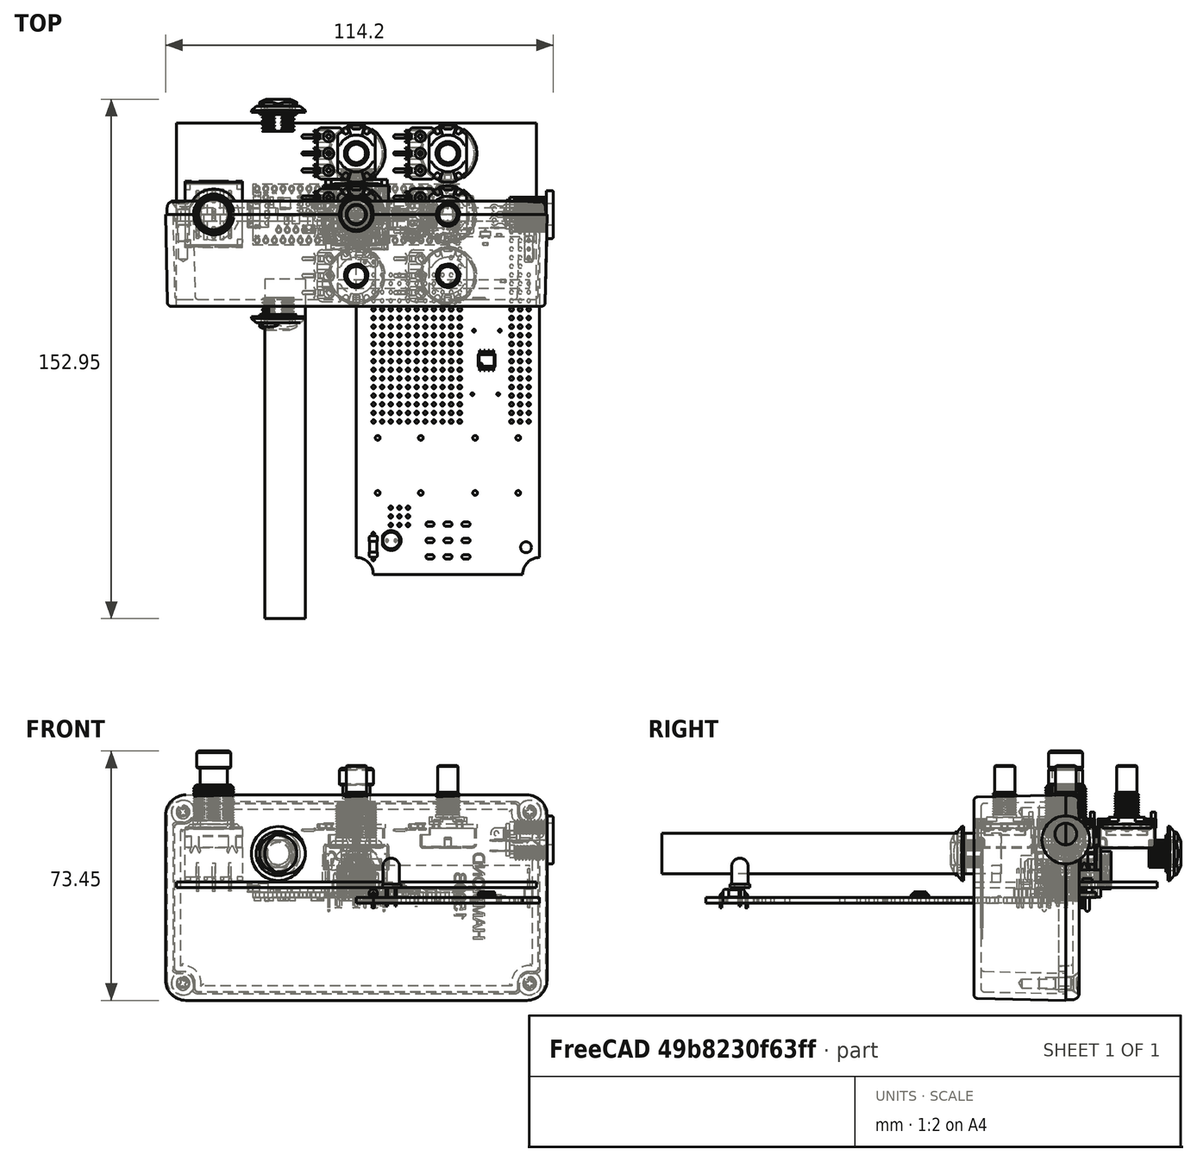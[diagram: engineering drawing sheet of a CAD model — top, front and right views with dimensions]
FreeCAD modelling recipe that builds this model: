
FCSTD DOCUMENT  (FreeCAD 0.19R24267 +148 (Git))
Label: 1590Balt
License: All rights reserved
LicenseURL: http://en.wikipedia.org/wiki/All_rights_reserved
objects: Part::Feature×58, App::Link×50, App::Part×9, Part::Box×3, Part::Compound2×1, Part::Cylinder×1, PartDesign::CoordinateSystem×1, Sketcher::SketchObject×1
note: 64 computed .brp shape members not serialized (recipe doc carries the construction recipe); baked Part::Feature solids carry a one-line shape summary decoded from their .brp

FEATURE [Part::Feature] Part__Feature  label="1590B BOX"
  Placement = pos=(0,0,0) rot=(-1,0,0;1.5708rad)
  shape: bbox 112.4 x 261 x 60.52 mm, 255 faces (baked)
FEATURE [Part::Feature] Part__Feature001  label="1590B-BS LID"
  Placement = pos=(0,0,0) rot=(0,0.707107,-0.707107;3.14159rad)
  shape: bbox 112.4 x 6.014 x 61.03 mm, 68 faces (baked)
FEATURE [Part::Feature] Part__Feature002  label="SC530 (screw #6-32X 1_2' FH)"
  Placement = pos=(-51.05,1.5362,25.25) rot=(0,1,0;0.650238rad)
  shape: bbox 6.871 x 11.85 x 6.871 mm, 25 faces (baked)
FEATURE [Part::Feature] Part__Feature003  label="SC530 (screw #6-32X 1_2' FH)001"
  Placement = pos=(-51.05,1.5362,-25.25) rot=(0,-1,0;0.529817rad)
  shape: bbox 6.871 x 11.85 x 6.871 mm, 25 faces (baked)
FEATURE [Part::Feature] Part__Feature004  label="SC530 (screw #6-32X 1_2' FH)002"
  Placement = pos=(51.05,1.5362,25.25) rot=(0,0,1;0rad)
  shape: bbox 6.871 x 11.85 x 6.871 mm, 25 faces (baked)
FEATURE [Part::Feature] Part__Feature005  label="SC530 (screw #6-32X 1_2' FH)003"
  Placement = pos=(51.05,1.5362,-25.25) rot=(0,0,1;0rad)
  shape: bbox 6.871 x 11.85 x 6.871 mm, 25 faces (baked)
FEATURE [App::Part] _590B  label="1590B"
  Group = -> [Part__Feature,Part__Feature001,Part__Feature002,Part__Feature003,Part__Feature004,Part__Feature005]
  Origin = -> Origin
  Placement = pos=(0,0,0) rot=(1,0,0;-1.5708rad)
FEATURE [Part::Feature] Part__Feature009  label="DC jack v1"
  Placement = pos=(58,0,17) rot=(0.57735,-0.57735,-0.57735;2.0944rad)
  shape: bbox 18.72 x 15.28 x 15.28 mm, 264 faces, 6 solids (baked)
FEATURE [Part::Feature] Part__Feature010  label="SF17020F-0302-21R-L v2"
  Placement = pos=(-42,0,5) rot=(0,0,-1;1.5708rad)
  shape: bbox 17.02 x 19.62 x 41.22 mm, 460 faces, 13 solids (baked)
FEATURE [Part::Box] Box  label="PCB"
  AttacherType = Attacher::AttachEngine3D
  Height = 1.6
  Length = 106
  Placement = pos=(-53,-27,3) rot=(0,0,1;0rad)
  Width = 54
FEATURE [Part::Box] Box002  label="header"
  AttacherType = Attacher::AttachEngine3D
  Height = 5
  Length = 61
  Placement = pos=(-10,-21.7,4.6) rot=(0,0,1;0rad)
  Width = 2.5
FEATURE [Part::Box] Box003  label="header001"
  AttacherType = Attacher::AttachEngine3D
  Height = 5
  Length = 61
  Placement = pos=(-10,-6.4,4.6) rot=(0,0,1;0rad)
  Width = 2.5
FEATURE [Part::Feature] Part__Feature037  label="RV16AF-20 v3"
  Placement = pos=(27,18,13) rot=(0,0,-1;1.5708rad)
  shape: bbox 24.95 x 17.82 x 24.32 mm, 272 faces, 6 solids (baked)
FEATURE [Part::Feature] Part__Feature038  label="RV16AF-20 v004"
  Placement = pos=(27,-6e-15,13) rot=(0,0,-1;1.5708rad)
  shape: bbox 24.95 x 17.82 x 24.32 mm, 272 faces, 6 solids (baked)
FEATURE [Part::Feature] Part__Feature039  label="RV16AF-20 v005"
  Placement = pos=(27,-18,13) rot=(0,0,-1;1.5708rad)
  shape: bbox 24.95 x 17.82 x 24.32 mm, 272 faces, 6 solids (baked)
FEATURE [Part::Feature] Part__Feature040  label="RV16AF-20 v006"
  Placement = pos=(4e-15,18,13) rot=(0,0,-1;1.5708rad)
  shape: bbox 24.95 x 17.82 x 24.32 mm, 272 faces, 6 solids (baked)
FEATURE [Part::Feature] Part__Feature041  label="RV16AF-20 v007"
  Placement = pos=(0,-1.2e-14,13) rot=(0,0,-1;1.5708rad)
  shape: bbox 24.95 x 17.82 x 24.32 mm, 272 faces, 6 solids (baked)
FEATURE [Part::Feature] Part__Feature042  label="RV16AF-20 v008"
  Placement = pos=(4e-15,-18,13) rot=(0,0,-1;1.5708rad)
  shape: bbox 24.95 x 17.82 x 24.32 mm, 272 faces, 6 solids (baked)
FEATURE [Part::Feature] Part__Feature043  label="NMJ nut washer v1"
  Placement = pos=(-23,-29.5,13) rot=(1,0,0;1.5708rad)
  shape: bbox 15.9 x 2.5 x 15.9 mm, 9 faces (baked)
FEATURE [Part::Feature] Part__Feature044  label="NMJ nut v1"
  Placement = pos=(-23,-34,13) rot=(-1,0,0;1.5708rad)
  shape: bbox 12.72 x 9.727 x 12.72 mm, 70 faces (baked)
FEATURE [Part::Feature] Part__Feature045  label="NMJ nut washer v002"
  Placement = pos=(-23,29.5,13) rot=(0,0.707107,0.707107;3.14159rad)
  shape: bbox 15.9 x 2.5 x 15.9 mm, 9 faces (baked)
FEATURE [Part::Feature] Solid
  shape: bbox 15 x 11.43 x 1.06 mm, 146 faces (baked)
FEATURE [Part::Feature] Solid001
  shape: bbox 62.51 x 17.83 x 5.318 mm, 3668 faces (baked)
FEATURE [Part::Compound2] Compound  label="CIRCUIT BOARD,TEENSY 4.1"
  Links = -> [Solid,Solid001]
  Placement = pos=(20.5,-12.8,9.6) rot=(0,0,1;3.14159rad)
FEATURE [Part::Feature] Part__Feature046  label="NMJ nut v002"
  Placement = pos=(-23,34,13) rot=(0,0.707107,-0.707107;3.14159rad)
  shape: bbox 12.72 x 9.727 x 12.72 mm, 70 faces (baked)
FEATURE [Part::Cylinder] Cylinder
  Angle = 360
  AttacherType = Attacher::AttachEngine3D
  Height = 100
  Placement = pos=(-21,-19,13) rot=(1,0,0;1.5708rad)
  Radius = 6
FEATURE [PartDesign::CoordinateSystem] Local_CS_9c2f
  AttacherType = Attacher::AttachEngine3D
  MapMode = 2
  Support = -> [X_Axis001]
FEATURE [Part::Feature] Pcb_9c2f
  shape: bbox 54 x 106 x 1.6 mm, 374 faces (baked)
FEATURE [Sketcher::SketchObject] PCB_Sketch_9c2f
  FullyConstrained = false
  sketch-geometry (8):
    g0: LineSegment StartX=5 StartY=-106 StartZ=0 EndX=49 EndY=-106 EndZ=0
    g1: LineSegment StartX=54 StartY=-5 StartZ=0 EndX=54 EndY=-101 EndZ=0
    g2: LineSegment StartX=5 StartY=0 StartZ=0 EndX=49 EndY=-2e-16 EndZ=0
    g3: LineSegment StartX=0 StartY=-101 StartZ=0 EndX=0 EndY=-5 EndZ=0
    g4: ArcOfCircle CenterX=54 CenterY=-106 CenterZ=0 NormalX=0 NormalY=0 NormalZ=-1 AngleXU=-6.42331e-08 Radius=5 StartAngle=0 EndAngle=1.5708
    g5: ArcOfCircle CenterX=54 CenterY=-3.21166e-07 CenterZ=0 NormalX=0 NormalY=0 NormalZ=-1 AngleXU=-1.5708 Radius=5 StartAngle=0 EndAngle=1.5708
    g6: ArcOfCircle CenterX=3.21166e-07 CenterY=-3.21166e-07 CenterZ=0 NormalX=0 NormalY=0 NormalZ=-1 AngleXU=3.14159 Radius=5 StartAngle=0 EndAngle=1.5708
    g7: ArcOfCircle CenterX=3.21166e-07 CenterY=-106 CenterZ=0 NormalX=0 NormalY=0 NormalZ=-1 AngleXU=1.5708 Radius=5 StartAngle=0 EndAngle=1.5708
  constraints (8):
    c: Coincident(g3,g7)
    c: Coincident(g3,g6)
    c: Coincident(g0,g7)
    c: Coincident(g2,g6)
    c: Coincident(g0,g4)
    c: Coincident(g2,g5)
    c: Coincident(g1,g4)
    c: Coincident(g1,g5)
FEATURE [App::Part] Board_Geoms_9c2f
  Group = -> [Pcb_9c2f,PCB_Sketch_9c2f]
  Origin = -> Origin002
FEATURE [Part::Feature] Shape  label="C21_C_0603_1608Metric_0bb367dbc1dc"
  Placement = pos=(38.05,-8.6,0) rot=(0,0,1;0rad)
  shape: bbox 1.6 x 0.8 x 0.8 mm, 28 faces (baked)
FEATURE [Part::Feature] Shape001  label="R19_R_0603_1608Metric_9eb986fb2b09"
  Placement = pos=(43.175,-19.6,0) rot=(0,0,1;3.14159rad)
  shape: bbox 1.6 x 0.8 x 0.45 mm, 26 faces (baked)
FEATURE [App::Link] C21_C_0603_1608Metric_0bb367dbc1dc_ln_  label="C7_C_0603_1608Metric_e1dc8168bc9f"
  LinkPlacement = pos=(45.125,-89.2,0) rot=(0,0,1;0rad)
  LinkedObject = -> Shape
  Placement = pos=(45.125,-89.2,0) rot=(0,0,1;0rad)
FEATURE [App::Link] R19_R_0603_1608Metric_9eb986fb2b09_ln_  label="R10_R_0603_1608Metric_166904e3697f"
  LinkPlacement = pos=(41.9,-49.1,0) rot=(0,0,-1;1.5708rad)
  LinkedObject = -> Shape001
  Placement = pos=(41.9,-49.1,0) rot=(0,0,-1;1.5708rad)
FEATURE [App::Link] R19_R_0603_1608Metric_9eb986fb2b09_ln_001  label="R23_R_0603_1608Metric_ba8bd125e6b8"
  LinkPlacement = pos=(41.7,-92.875,0) rot=(0,0,1;1.5708rad)
  LinkedObject = -> Shape001
  Placement = pos=(41.7,-92.875,0) rot=(0,0,1;1.5708rad)
FEATURE [Part::Feature] Part__Feature047  label="NMJ4HCD2 v9"
  shape: bbox 15.98 x 4 x 17.64 mm, 30 faces (baked)
FEATURE [Part::Feature] Part__Feature048  label="NMJ4HCD2 v010"
  shape: bbox 4.005 x 4.005 x 13.14 mm, 15 faces (baked)
FEATURE [Part::Feature] Part__Feature049  label="NMJ4HCD2 v011"
  shape: bbox 15.98 x 4 x 17.64 mm, 30 faces (baked)
FEATURE [Part::Feature] Part__Feature050  label="NMJ4HCD2 v012"
  shape: bbox 4.005 x 4.005 x 13.14 mm, 15 faces (baked)
FEATURE [Part::Feature] Part__Feature051  label="NMJ4HCD2 v013"
  shape: bbox 18.22 x 26.85 x 16 mm, 172 faces (baked)
FEATURE [App::Part] NMJ4HCD2_v9  label="J14_NMJ4HCD2 v014_e41c6919c46c"
  Group = -> [Part__Feature047,Part__Feature048,Part__Feature049,Part__Feature050,Part__Feature051]
  Origin = -> Origin008
  Placement = pos=(41.35,-73.87,0) rot=(0,0,-1;1.5708rad)
FEATURE [App::Link] C21_C_0603_1608Metric_0bb367dbc1dc_ln_001  label="C22_C_0603_1608Metric_e366c6b039dc"
  LinkPlacement = pos=(33.975,-16.1,0) rot=(0,0,1;3.14159rad)
  LinkedObject = -> Shape
  Placement = pos=(33.975,-16.1,0) rot=(0,0,1;3.14159rad)
FEATURE [Part::Feature] Shape002  label="D2_D_SMA_29150ae1a044"
  Placement = pos=(16.3,-6.4,0) rot=(0,0,1;3.14159rad)
  shape: bbox 5 x 2.7 x 2.22 mm, 41 faces (baked)
FEATURE [App::Link] R19_R_0603_1608Metric_9eb986fb2b09_ln_002  label="R17_R_0603_1608Metric_a49cdc6c4dda"
  LinkPlacement = pos=(35.25,-30.85,0) rot=(0,0,1;1.5708rad)
  LinkedObject = -> Shape001
  Placement = pos=(35.25,-30.85,0) rot=(0,0,1;1.5708rad)
FEATURE [Part::Feature] Shape003  label="R25_R_Axial_DIN0207_L63mm_D25mm_P762mm_Horizontal_27912f56e347"
  Placement = pos=(5,-101.6,0) rot=(0,0,1;1.5708rad)
  shape: bbox 2.706 x 8.418 x 5.603 mm, 15 faces (baked)
FEATURE [Part::Feature] Shape004  label="U3_SOIC_8_39x49mm_P127mm_f811e89be06e"
  Placement = pos=(38.405,-42.975,0) rot=(0,0,1;1.5708rad)
  shape: bbox 4.9 x 6 x 1.75 mm, 156 faces (baked)
FEATURE [App::Link] R19_R_0603_1608Metric_9eb986fb2b09_ln_003  label="R20_R_0603_1608Metric_24a8fece7dd1"
  LinkPlacement = pos=(42.825,-8.2,0) rot=(0,0,1;0rad)
  LinkedObject = -> Shape001
  Placement = pos=(42.825,-8.2,0) rot=(0,0,1;0rad)
FEATURE [App::Link] R19_R_0603_1608Metric_9eb986fb2b09_ln_004  label="R16_R_0603_1608Metric_ea3f6324f917"
  LinkPlacement = pos=(40.75,-30.85,0) rot=(0,0,1;1.5708rad)
  LinkedObject = -> Shape001
  Placement = pos=(40.75,-30.85,0) rot=(0,0,1;1.5708rad)
FEATURE [Part::Feature] Shape005  label="FB1_L_0603_1608Metric_f1a17431d369"
  Placement = pos=(41.9875,-6.1,0) rot=(0,0,1;3.14159rad)
  shape: bbox 1.6 x 0.8 x 0.8 mm, 28 faces (baked)
FEATURE [App::Link] C21_C_0603_1608Metric_0bb367dbc1dc_ln_002  label="C4_C_0603_1608Metric_83afc9113bc5"
  LinkPlacement = pos=(20.275,-14,0) rot=(0,0,1;3.14159rad)
  LinkedObject = -> Shape
  Placement = pos=(20.275,-14,0) rot=(0,0,1;3.14159rad)
FEATURE [App::Link] U3_SOIC_8_39x49mm_P127mm_f811e89be06e_ln_  label="U2_SOIC_8_39x49mm_P127mm_fd0538945ea7"
  LinkPlacement = pos=(14.275,-11.155,0) rot=(0,0,1;0rad)
  LinkedObject = -> Shape004
  Placement = pos=(14.275,-11.155,0) rot=(0,0,1;0rad)
FEATURE [App::Link] C21_C_0603_1608Metric_0bb367dbc1dc_ln_003  label="C8_C_0603_1608Metric_fb45835040b8"
  LinkPlacement = pos=(48.225,-89.2,0) rot=(0,0,1;0rad)
  LinkedObject = -> Shape
  Placement = pos=(48.225,-89.2,0) rot=(0,0,1;0rad)
FEATURE [App::Link] R19_R_0603_1608Metric_9eb986fb2b09_ln_005  label="R15_R_0603_1608Metric_a228be05d594"
  LinkPlacement = pos=(39.575,-38.4,0) rot=(0,0,1;3.14159rad)
  LinkedObject = -> Shape001
  Placement = pos=(39.575,-38.4,0) rot=(0,0,1;3.14159rad)
FEATURE [App::Link] R19_R_0603_1608Metric_9eb986fb2b09_ln_006  label="R18_R_0603_1608Metric_52eb841925d1"
  LinkPlacement = pos=(43.175,-22.2,0) rot=(0,0,1;3.14159rad)
  LinkedObject = -> Shape001
  Placement = pos=(43.175,-22.2,0) rot=(0,0,1;3.14159rad)
FEATURE [App::Link] R19_R_0603_1608Metric_9eb986fb2b09_ln_007  label="R3_R_0603_1608Metric_e7e518a56965"
  LinkPlacement = pos=(24.75,-14,0) rot=(0,0,1;0rad)
  LinkedObject = -> Shape001
  Placement = pos=(24.75,-14,0) rot=(0,0,1;0rad)
FEATURE [Part::Feature] Shape006  label="J12_PinHeader_1x03_P254mm_Vertical_9115b0f02c0e"
  Placement = pos=(50.8,-12.7,0) rot=(0,0,1;3.14159rad)
  shape: bbox 2.54 x 7.62 x 11.54 mm, 76 faces (baked)
FEATURE [Part::Feature] Shape007  label="C1_C_0805_2012Metric_d96382e3b60e"
  Placement = pos=(8.775,-9.405,0) rot=(0,0,1;1.5708rad)
  shape: bbox 1.25 x 2 x 1.25 mm, 28 faces (baked)
FEATURE [Part::Feature] Shape008  label="J11_PinHeader_1x02_P254mm_Vertical_0465e6913453"
  Placement = pos=(5.08,-13.97,0) rot=(0,0,-1;1.5708rad)
  shape: bbox 5.08 x 2.54 x 11.54 mm, 52 faces (baked)
FEATURE [App::Link] C21_C_0603_1608Metric_0bb367dbc1dc_ln_004  label="C16_C_0603_1608Metric_a1ca38057839"
  LinkPlacement = pos=(39.15,-27.775,0) rot=(0,0,-1;1.5708rad)
  LinkedObject = -> Shape
  Placement = pos=(39.15,-27.775,0) rot=(0,0,-1;1.5708rad)
FEATURE [Part::Feature] Shape009  label="U4_SOT_23_d04ffcebcd1d"
  Placement = pos=(38.025,-5.6625,0) rot=(0,0,1;1.5708rad)
  shape: bbox 3 x 2.5 x 1.2 mm, 76 faces (baked)
FEATURE [App::Link] R19_R_0603_1608Metric_9eb986fb2b09_ln_008  label="R11_R_0603_1608Metric_31f96d638436"
  LinkPlacement = pos=(42,-39.175,0) rot=(0,0,1;1.5708rad)
  LinkedObject = -> Shape001
  Placement = pos=(42,-39.175,0) rot=(0,0,1;1.5708rad)
FEATURE [App::Link] R19_R_0603_1608Metric_9eb986fb2b09_ln_009  label="R13_R_0603_1608Metric_b8c1c6806a0d"
  LinkPlacement = pos=(39,-48.2,0) rot=(0,0,1;3.14159rad)
  LinkedObject = -> Shape001
  Placement = pos=(39,-48.2,0) rot=(0,0,1;3.14159rad)
FEATURE [App::Link] U4_SOT_23_d04ffcebcd1d_ln_  label="D4_SOT_23_4c7b28e5f7f7"
  LinkPlacement = pos=(36.2,-24.2375,0) rot=(0,0,1;1.5708rad)
  LinkedObject = -> Shape009
  Placement = pos=(36.2,-24.2375,0) rot=(0,0,1;1.5708rad)
FEATURE [App::Link] R19_R_0603_1608Metric_9eb986fb2b09_ln_010  label="R22_R_0603_1608Metric_5d6f341969fb"
  LinkPlacement = pos=(41.7,-89.775,0) rot=(0,0,1;1.5708rad)
  LinkedObject = -> Shape001
  Placement = pos=(41.7,-89.775,0) rot=(0,0,1;1.5708rad)
FEATURE [App::Link] C21_C_0603_1608Metric_0bb367dbc1dc_ln_005  label="C26_C_0603_1608Metric_d3c024f64aa1"
  LinkPlacement = pos=(40.1,-86.725,0) rot=(0,0,-1;1.5708rad)
  LinkedObject = -> Shape
  Placement = pos=(40.1,-86.725,0) rot=(0,0,-1;1.5708rad)
FEATURE [App::Link] R19_R_0603_1608Metric_9eb986fb2b09_ln_011  label="R7_R_0603_1608Metric_485696e41206"
  LinkPlacement = pos=(48.225,-86,0) rot=(0,0,1;0rad)
  LinkedObject = -> Shape001
  Placement = pos=(48.225,-86,0) rot=(0,0,1;0rad)
FEATURE [App::Link] C21_C_0603_1608Metric_0bb367dbc1dc_ln_006  label="C3_C_0603_1608Metric_49f07377d576"
  LinkPlacement = pos=(9.275,-13.88,0) rot=(0,0,-1;1.5708rad)
  LinkedObject = -> Shape
  Placement = pos=(9.275,-13.88,0) rot=(0,0,-1;1.5708rad)
FEATURE [App::Link] U4_SOT_23_d04ffcebcd1d_ln_001  label="D3_SOT_23_e7ea7a7a331e"
  LinkPlacement = pos=(39.8,-24.2375,0) rot=(0,0,1;1.5708rad)
  LinkedObject = -> Shape009
  Placement = pos=(39.8,-24.2375,0) rot=(0,0,1;1.5708rad)
FEATURE [App::Link] C21_C_0603_1608Metric_0bb367dbc1dc_ln_007  label="C23_C_0603_1608Metric_e1f06f9a68ca"
  LinkPlacement = pos=(32.8,-12.6,0) rot=(0,0,1;1.5708rad)
  LinkedObject = -> Shape
  Placement = pos=(32.8,-12.6,0) rot=(0,0,1;1.5708rad)
FEATURE [App::Link] C21_C_0603_1608Metric_0bb367dbc1dc_ln_008  label="C24_C_0603_1608Metric_7525f09e29e1"
  LinkPlacement = pos=(34.5,-13,0) rot=(0,0,1;1.5708rad)
  LinkedObject = -> Shape
  Placement = pos=(34.5,-13,0) rot=(0,0,1;1.5708rad)
FEATURE [App::Link] R19_R_0603_1608Metric_9eb986fb2b09_ln_012  label="R8_R_0603_1608Metric_af00bf1825cb"
  LinkPlacement = pos=(45.125,-87.6,0) rot=(0,0,1;0rad)
  LinkedObject = -> Shape001
  Placement = pos=(45.125,-87.6,0) rot=(0,0,1;0rad)
FEATURE [App::Link] C21_C_0603_1608Metric_0bb367dbc1dc_ln_009  label="C19_C_0603_1608Metric_ce09af4a767a"
  LinkPlacement = pos=(43.3,-14.5,0) rot=(0,0,-1;1.5708rad)
  LinkedObject = -> Shape
  Placement = pos=(43.3,-14.5,0) rot=(0,0,-1;1.5708rad)
FEATURE [App::Link] R19_R_0603_1608Metric_9eb986fb2b09_ln_013  label="R6_R_0603_1608Metric_cb2465086048"
  LinkPlacement = pos=(45.125,-86,0) rot=(0,0,1;0rad)
  LinkedObject = -> Shape001
  Placement = pos=(45.125,-86,0) rot=(0,0,1;0rad)
FEATURE [App::Link] C21_C_0603_1608Metric_0bb367dbc1dc_ln_010  label="C13_C_0603_1608Metric_1fc0c24e4ce7"
  LinkPlacement = pos=(34.8,-42.575,0) rot=(0,0,1;1.5708rad)
  LinkedObject = -> Shape
  Placement = pos=(34.8,-42.575,0) rot=(0,0,1;1.5708rad)
FEATURE [App::Link] R19_R_0603_1608Metric_9eb986fb2b09_ln_014  label="R21_R_0603_1608Metric_91259863e668"
  LinkPlacement = pos=(40.1,-89.775,0) rot=(0,0,1;1.5708rad)
  LinkedObject = -> Shape001
  Placement = pos=(40.1,-89.775,0) rot=(0,0,1;1.5708rad)
FEATURE [App::Link] J14_NMJ4HCD2_v014_e41c6919c46c_ln_  label="J15_NMJ4HCD2 v014_a7057465bf2c"
  LinkPlacement = pos=(12.65,-73.9,0) rot=(0,0,1;1.5708rad)
  LinkedObject = -> NMJ4HCD2_v9
  Placement = pos=(12.65,-73.9,0) rot=(0,0,1;1.5708rad)
FEATURE [App::Link] C21_C_0603_1608Metric_0bb367dbc1dc_ln_011  label="C17_C_0603_1608Metric_fe6673debad5"
  LinkPlacement = pos=(36.85,-27.8,0) rot=(0,0,-1;1.5708rad)
  LinkedObject = -> Shape
  Placement = pos=(36.85,-27.8,0) rot=(0,0,-1;1.5708rad)
FEATURE [App::Link] C21_C_0603_1608Metric_0bb367dbc1dc_ln_012  label="C14_C_0603_1608Metric_e5ab031fdba9"
  LinkPlacement = pos=(39.15,-30.85,0) rot=(0,0,-1;1.5708rad)
  LinkedObject = -> Shape
  Placement = pos=(39.15,-30.85,0) rot=(0,0,-1;1.5708rad)
FEATURE [App::Link] R19_R_0603_1608Metric_9eb986fb2b09_ln_015  label="R1_R_0603_1608Metric_5eedb9b17a7b"
  LinkPlacement = pos=(21.5,-11.425,0) rot=(0,0,-1;1.5708rad)
  LinkedObject = -> Shape001
  Placement = pos=(21.5,-11.425,0) rot=(0,0,-1;1.5708rad)
FEATURE [App::Link] R19_R_0603_1608Metric_9eb986fb2b09_ln_016  label="R9_R_0603_1608Metric_28e75ca2e0db"
  LinkPlacement = pos=(48.225,-87.6,0) rot=(0,0,1;0rad)
  LinkedObject = -> Shape001
  Placement = pos=(48.225,-87.6,0) rot=(0,0,1;0rad)
FEATURE [App::Link] C21_C_0603_1608Metric_0bb367dbc1dc_ln_013  label="C11_C_0603_1608Metric_8c769205a595"
  LinkPlacement = pos=(39,-50,0) rot=(0,0,1;3.14159rad)
  LinkedObject = -> Shape
  Placement = pos=(39,-50,0) rot=(0,0,1;3.14159rad)
FEATURE [App::Link] C21_C_0603_1608Metric_0bb367dbc1dc_ln_014  label="C25_C_0603_1608Metric_e6f2cbd31909"
  LinkPlacement = pos=(41.7,-86.725,0) rot=(0,0,-1;1.5708rad)
  LinkedObject = -> Shape
  Placement = pos=(41.7,-86.725,0) rot=(0,0,-1;1.5708rad)
FEATURE [Part::Feature] Shape010  label="C6_C_1210_3225Metric_0ee3ade16b7e"
  Placement = pos=(22.125,-2.1,0) rot=(0,0,1;3.14159rad)
  shape: bbox 3.2 x 2.5 x 2.5 mm, 28 faces (baked)
FEATURE [App::Link] C21_C_0603_1608Metric_0bb367dbc1dc_ln_015  label="C18_C_0603_1608Metric_abef51ed0170"
  LinkPlacement = pos=(35.575,-6.025,0) rot=(0,0,1;1.5708rad)
  LinkedObject = -> Shape
  Placement = pos=(35.575,-6.025,0) rot=(0,0,1;1.5708rad)
FEATURE [App::Link] C21_C_0603_1608Metric_0bb367dbc1dc_ln_016  label="C9_C_0603_1608Metric_aab1e25b7470"
  LinkPlacement = pos=(42,-45.375,0) rot=(0,0,-1;1.5708rad)
  LinkedObject = -> Shape
  Placement = pos=(42,-45.375,0) rot=(0,0,-1;1.5708rad)
FEATURE [Part::Feature] Shape011  label="D1_D_DO-41_SOD81_P10.16mm_Horizontal_a094bea6c747"
  Placement = pos=(7.5,-2.25,0) rot=(0,0,1;0rad)
  shape: bbox 11.16 x 2.72 x 5.71 mm, 15 faces (baked)
FEATURE [App::Link] R19_R_0603_1608Metric_9eb986fb2b09_ln_017  label="R2_R_0603_1608Metric_43e694a8c211"
  LinkPlacement = pos=(24,-11.5,0) rot=(0,0,-1;1.5708rad)
  LinkedObject = -> Shape001
  Placement = pos=(24,-11.5,0) rot=(0,0,-1;1.5708rad)
FEATURE [Part::Feature] Shape012  label="D5_LED_D5.0mm_fd43042c8943"
  Placement = pos=(9,-96,0) rot=(0,0,1;0rad)
  shape: bbox 5.4 x 5.8 x 14.1 mm, 16 faces (baked)
FEATURE [Part::Feature] Part__Feature052  label="SF17020F-0302-21R-L v003"
  shape: bbox 19.6 x 17 x 15.2 mm, 123 faces (baked)
FEATURE [Part::Feature] Part__Feature006  label="SF17020F-0302-21R-L v004"
  shape: bbox 19 x 17 x 9.306 mm, 65 faces (baked)
FEATURE [Part::Feature] Part__Feature007  label="SF17020F-0302-21R-L v005"
  shape: bbox 12.62 x 12.13 x 13.01 mm, 67 faces (baked)
FEATURE [Part::Feature] Part__Feature008  label="SF17020F-0302-21R-L v006"
  shape: bbox 10 x 10 x 23 mm, 7 faces (baked)
FEATURE [Part::Feature] Part__Feature053  label="SF17020F-0302-21R-L v007"
  shape: bbox 3.4 x 0.8 x 8.2 mm, 22 faces (baked)
FEATURE [Part::Feature] Part__Feature054  label="SF17020F-0302-21R-L v008"
  shape: bbox 3.4 x 0.8 x 8.2 mm, 22 faces (baked)
FEATURE [Part::Feature] Part__Feature011  label="SF17020F-0302-21R-L v009"
  shape: bbox 3.4 x 0.8 x 8.2 mm, 22 faces (baked)
FEATURE [Part::Feature] Part__Feature012  label="SF17020F-0302-21R-L v010"
  shape: bbox 3.4 x 0.8 x 8.2 mm, 22 faces (baked)
FEATURE [Part::Feature] Part__Feature013  label="SF17020F-0302-21R-L v011"
  shape: bbox 3.4 x 0.8 x 8.2 mm, 22 faces (baked)
FEATURE [Part::Feature] Part__Feature014  label="SF17020F-0302-21R-L v012"
  shape: bbox 3.4 x 0.8 x 8.2 mm, 22 faces (baked)
FEATURE [Part::Feature] Part__Feature015  label="SF17020F-0302-21R-L v013"
  shape: bbox 3.4 x 0.8 x 8.2 mm, 22 faces (baked)
FEATURE [Part::Feature] Part__Feature016  label="SF17020F-0302-21R-L v014"
  shape: bbox 3.4 x 0.8 x 8.2 mm, 22 faces (baked)
FEATURE [Part::Feature] Part__Feature017  label="SF17020F-0302-21R-L v015"
  shape: bbox 3.4 x 0.8 x 8.2 mm, 22 faces (baked)
FEATURE [App::Part] SF17020F_0302_21R_L_v2  label="SW1_SF17020F-0302-21R-L v015_e1433bf92f28"
  Group = -> [Part__Feature052,Part__Feature006,Part__Feature007,Part__Feature008,Part__Feature053,Part__Feature054,Part__Feature011,Part__Feature012,Part__Feature013,Part__Feature014,Part__Feature015,Part__Feature016,Part__Feature017]
  Origin = -> Origin009
  Placement = pos=(27,-96,0) rot=(0,0,1;0rad)
FEATURE [App::Link] C21_C_0603_1608Metric_0bb367dbc1dc_ln_017  label="C2_C_0603_1608Metric_cd6c32cfebb9"
  LinkPlacement = pos=(20,-9,0) rot=(0,0,1;3.14159rad)
  LinkedObject = -> Shape
  Placement = pos=(20,-9,0) rot=(0,0,1;3.14159rad)
FEATURE [App::Link] R19_R_0603_1608Metric_9eb986fb2b09_ln_018  label="R5_R_0603_1608Metric_4f759ee281ee"
  LinkPlacement = pos=(48.215,-90.8,0) rot=(0,0,1;0rad)
  LinkedObject = -> Shape001
  Placement = pos=(48.215,-90.8,0) rot=(0,0,1;0rad)
FEATURE [App::Link] C21_C_0603_1608Metric_0bb367dbc1dc_ln_018  label="C15_C_0603_1608Metric_10773ecf366c"
  LinkPlacement = pos=(36.85,-30.85,0) rot=(0,0,1;1.5708rad)
  LinkedObject = -> Shape
  Placement = pos=(36.85,-30.85,0) rot=(0,0,1;1.5708rad)
FEATURE [App::Link] R19_R_0603_1608Metric_9eb986fb2b09_ln_019  label="R4_R_0603_1608Metric_4d4d8acdd4b8"
  LinkPlacement = pos=(45.125,-90.8,0) rot=(0,0,1;0rad)
  LinkedObject = -> Shape001
  Placement = pos=(45.125,-90.8,0) rot=(0,0,1;0rad)
FEATURE [App::Link] C21_C_0603_1608Metric_0bb367dbc1dc_ln_019  label="C12_C_0603_1608Metric_c4197c914b0f"
  LinkPlacement = pos=(39.575,-36.8,0) rot=(0,0,1;3.14159rad)
  LinkedObject = -> Shape
  Placement = pos=(39.575,-36.8,0) rot=(0,0,1;3.14159rad)
FEATURE [App::Link] C21_C_0603_1608Metric_0bb367dbc1dc_ln_020  label="C20_C_0603_1608Metric_cf10582c946e"
  LinkPlacement = pos=(41.5,-14.5,0) rot=(0,0,-1;1.5708rad)
  LinkedObject = -> Shape
  Placement = pos=(41.5,-14.5,0) rot=(0,0,-1;1.5708rad)
FEATURE [App::Link] R19_R_0603_1608Metric_9eb986fb2b09_ln_020  label="R24_R_0603_1608Metric_f990cb61f366"
  LinkPlacement = pos=(40.1,-92.875,0) rot=(0,0,1;1.5708rad)
  LinkedObject = -> Shape001
  Placement = pos=(40.1,-92.875,0) rot=(0,0,1;1.5708rad)
FEATURE [App::Link] C21_C_0603_1608Metric_0bb367dbc1dc_ln_021  label="C10_C_0603_1608Metric_7d06bfc1782d"
  LinkPlacement = pos=(42,-42.325,0) rot=(0,0,1;1.5708rad)
  LinkedObject = -> Shape
  Placement = pos=(42,-42.325,0) rot=(0,0,1;1.5708rad)
FEATURE [App::Link] C21_C_0603_1608Metric_0bb367dbc1dc_ln_022  label="C5_C_0603_1608Metric_fa0419f52b85"
  LinkPlacement = pos=(19.25,-11.525,0) rot=(0,0,1;1.5708rad)
  LinkedObject = -> Shape
  Placement = pos=(19.25,-11.525,0) rot=(0,0,1;1.5708rad)
FEATURE [App::Part] Top_9c2f
  Group = -> [Shape,Shape001,C21_C_0603_1608Metric_0bb367dbc1dc_ln_,R19_R_0603_1608Metric_9eb986fb2b09_ln_,R19_R_0603_1608Metric_9eb986fb2b09_ln_001,NMJ4HCD2_v9,C21_C_0603_1608Metric_0bb367dbc1dc_ln_001,Shape002,R19_R_0603_1608Metric_9eb986fb2b09_ln_002,Shape003,Shape004,R19_R_0603_1608Metric_9eb986fb2b09_ln_003,R19_R_0603_1608Metric_9eb986fb2b09_ln_004,Shape005,C21_C_0603_1608Metric_0bb367dbc1dc_ln_002,+48 more]
  Origin = -> Origin004
FEATURE [App::Link] R25_R_Axial_DIN0207_L63mm_D25mm_P762mm_Horizontal_27912f56e347_ln_  label="R14_R_Axial_DIN0207_L63mm_D25mm_P762mm_Horizontal_0b51a62667fa"
  LinkPlacement = pos=(42.3,-34.2,-1.6) rot=(0,1,0;3.14159rad)
  LinkedObject = -> Shape003
  Placement = pos=(42.3,-34.2,-1.6) rot=(0,1,0;3.14159rad)
FEATURE [App::Link] R25_R_Axial_DIN0207_L63mm_D25mm_P762mm_Horizontal_27912f56e347_ln_001  label="R12_R_Axial_DIN0207_L63mm_D25mm_P762mm_Horizontal_41a4d0aac9ac"
  LinkPlacement = pos=(41.81,-52.9,-1.6) rot=(0,1,0;3.14159rad)
  LinkedObject = -> Shape003
  Placement = pos=(41.81,-52.9,-1.6) rot=(0,1,0;3.14159rad)
FEATURE [App::Part] Bot_9c2f
  Group = -> [R25_R_Axial_DIN0207_L63mm_D25mm_P762mm_Horizontal_27912f56e347_ln_,R25_R_Axial_DIN0207_L63mm_D25mm_P762mm_Horizontal_27912f56e347_ln_001]
  Origin = -> Origin010
FEATURE [App::Part] Step_Models_9c2f
  Group = -> [Top_9c2f,Bot_9c2f]
  Origin = -> Origin003
FEATURE [App::Part] Board_9c2f  label="kicad_pcb"
  Group = -> [Local_CS_9c2f,Board_Geoms_9c2f,Step_Models_9c2f]
  Origin = -> Origin001
  Placement = pos=(53,27,4.6) rot=(0,0,1;4.71239rad)
FEATURE [Part::Feature] Part__Feature055  label="DC jack external v5"
  shape: bbox 7.166 x 0.5064 x 11.21 mm, 32 faces (baked)
FEATURE [Part::Feature] Part__Feature056  label="DC jack external v006"
  shape: bbox 3.572 x 3.572 x 11.8 mm, 15 faces (baked)
FEATURE [Part::Feature] Part__Feature057  label="DC jack external v007"
  shape: bbox 7.172 x 3.812 x 15.71 mm, 33 faces (baked)
FEATURE [Part::Feature] Part__Feature058  label="DC jack external v008"
  shape: bbox 8.6 x 9.3 x 1 mm, 23 faces (baked)
FEATURE [Part::Feature] Part__Feature059  label="DC jack external v009"
  shape: bbox 5.951 x 3.331 x 4.901 mm, 40 faces (baked)
FEATURE [Part::Feature] Part__Feature060  label="DC jack external v010"
  shape: bbox 16.25 x 16.25 x 12.51 mm, 124 faces (baked)
FEATURE [App::Part] DC_jack_external_v5  label="DC jack external v011"
  Group = -> [Part__Feature055,Part__Feature056,Part__Feature057,Part__Feature058,Part__Feature059,Part__Feature060]
  Origin = -> Origin011
  Placement = pos=(61.8,0,17) rot=(0,1,0;4.71239rad)
